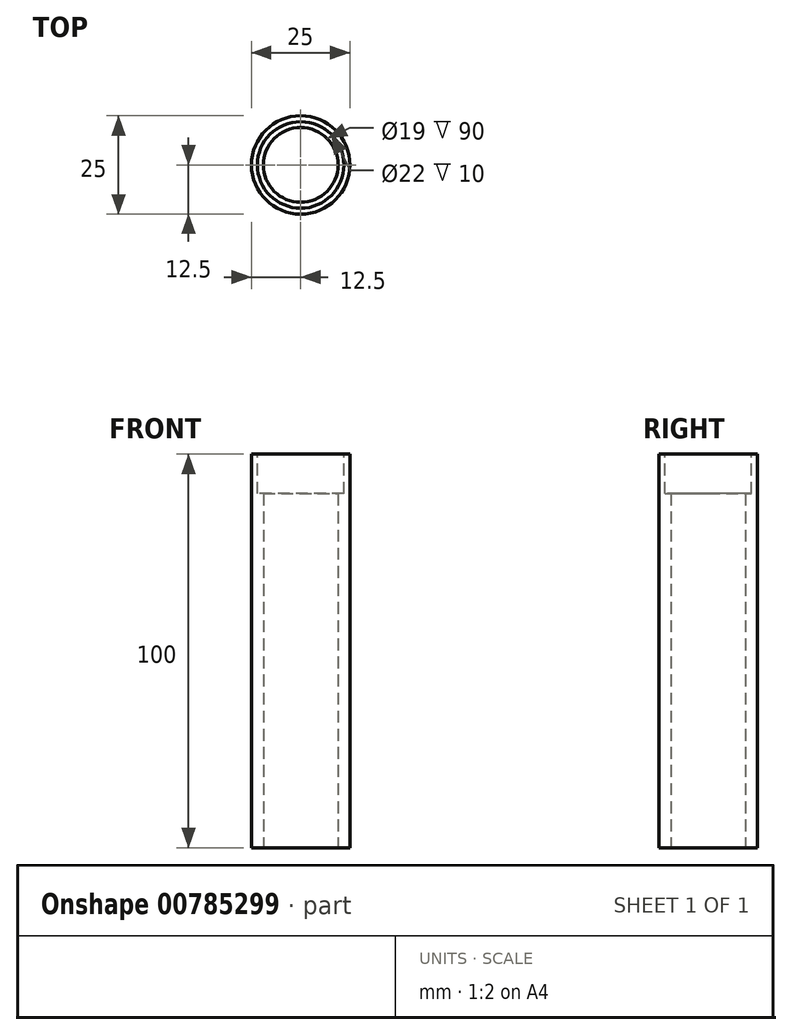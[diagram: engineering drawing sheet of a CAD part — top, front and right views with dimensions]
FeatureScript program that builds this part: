
annotation { "Feature Type Name" : "Feature", "Feature Type Description" : "" }
export const myFeature = defineFeature(function(context is Context, id is Id, definition is map)
    precondition{}
    {
        {
            var Q0;
            Q0=qCreatedBy(makeId("Top.planeOp"),FACE);
            var sketch = newSketch(context, id + "F0", { "sketchPlane" : qUnion([Q0])});
            skCircle(sketch, "E0", {"center": v(0, 0) * mm, "radius": 12.5 * mm});
            skSolve(sketch);
        }
        {
            var Q0;
            Q0=makeQuery(id+"F0.imprint","IMPRINT",FACE,{"disambiguationData":[TD([[makeQuery(id+"F0.imprint","IMPRINT",EDGE,{"derivedFrom":sQuery(id+"F0.wireOp",EDGE,"E0")}),1.0]])]});
            extrude(context, id + "F1", {"entities" : qUnion([Q0]), "depth" : 100 * mm, "offsetDistance" : 25.4 * mm});
        }
        {
            var Q0;
            Q0=makeQuery(id+"F1.opExtrude","CAP_FACE",FACE,{"disambiguationData":[OSD([sQuery(id+"F0.wireOp",EDGE,"E0")])],"isStart":true});
            var sketch = newSketch(context, id + "F2", { "sketchPlane" : qUnion([Q0])});
            skCircle(sketch, "E1", {"center": v(0, 0) * mm, "radius": 9.5 * mm});
            skSolve(sketch);
        }
        {
            var Q0;
            Q0 = qSketchRegion(id + "F2", true);
            extrude(context, id + "F3", {"entities" : qUnion([Q0]), "operationType" : NewBodyOperationType.REMOVE, "oppositeDirection" : true, "depth" : 90 * mm, "offsetDistance" : 25.4 * mm, "hasSecondDirection" : true, "secondDirectionOppositeDirection" : false, "secondDirectionDepth" : 101.35 * mm});
        }
        {
            var Q0;
            Q0=makeQuery(id+"F1.opExtrude","CAP_FACE",FACE,{"disambiguationData":[OSD([sQuery(id+"F0.wireOp",EDGE,"E0")])],"isStart":false});
            var sketch = newSketch(context, id + "F4", { "sketchPlane" : qUnion([Q0])});
            skCircle(sketch, "E2", {"center": v(0, 0) * mm, "radius": 11 * mm});
            skSolve(sketch);
        }
        {
            var Q0;
            Q0 = qSketchRegion(id + "F4", true);
            extrude(context, id + "F5", {"entities" : qUnion([Q0]), "operationType" : NewBodyOperationType.REMOVE, "oppositeDirection" : true, "depth" : 10 * mm, "offsetDistance" : 25.4 * mm, "hasSecondDirection" : true, "secondDirectionOppositeDirection" : false, "secondDirectionDepth" : 25.4 * mm});
        }
    });
